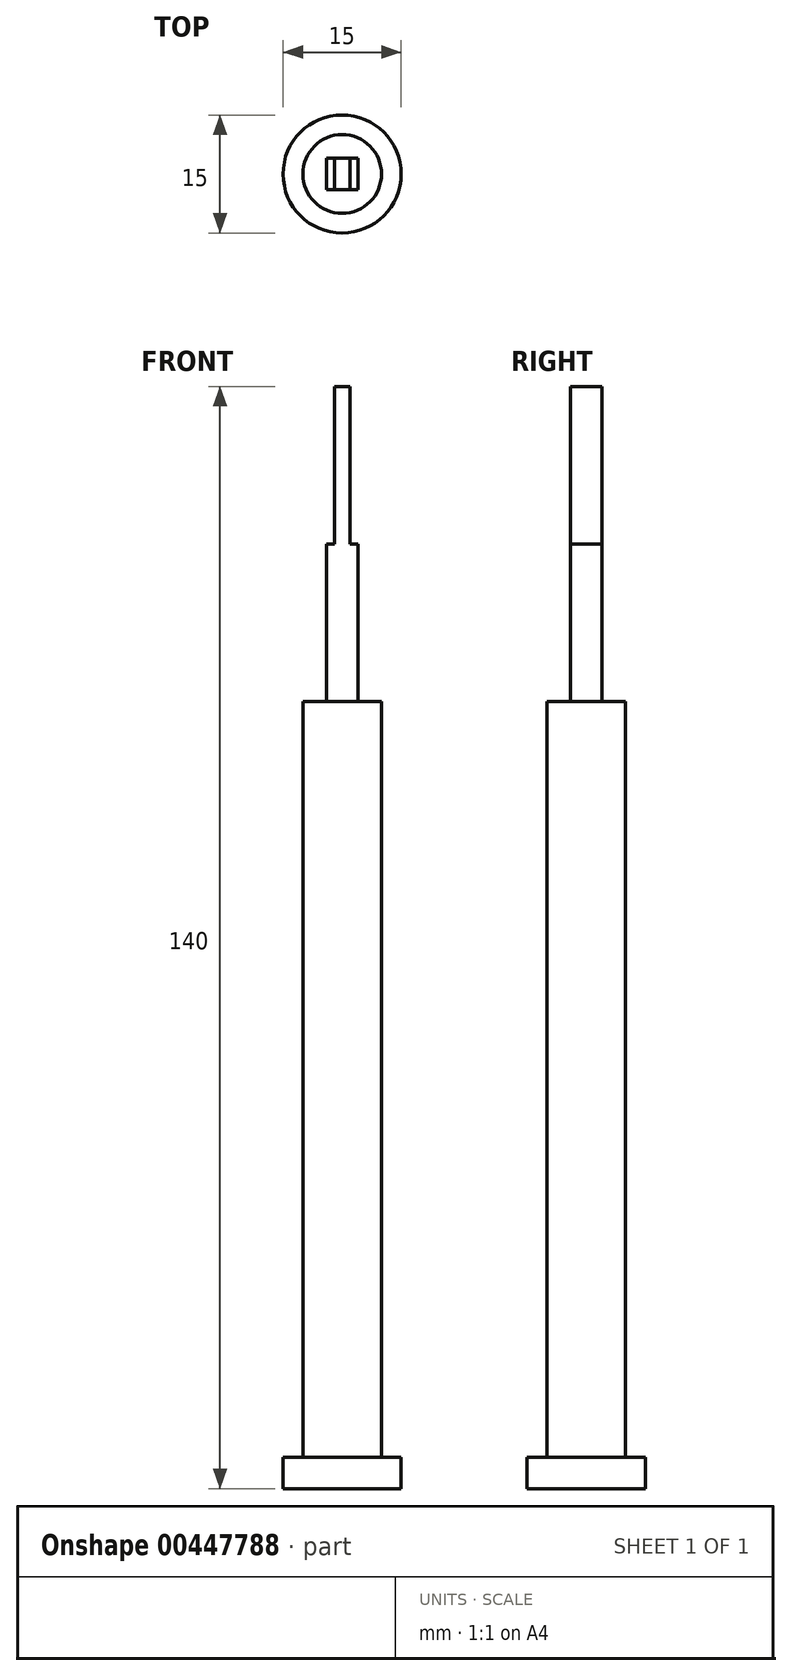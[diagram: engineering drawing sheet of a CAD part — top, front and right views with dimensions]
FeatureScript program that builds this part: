
annotation { "Feature Type Name" : "Feature", "Feature Type Description" : "" }
export const myFeature = defineFeature(function(context is Context, id is Id, definition is map)
    precondition{}
    {
        {
            var Q0;
            Q0=qCreatedBy(makeId("Top.planeOp"),FACE);
            var sketch = newSketch(context, id + "F0", { "sketchPlane" : qUnion([Q0])});
            skCircle(sketch, "E0", {"center": v(0, 0) * mm, "radius": 7.5 * mm});
            skSolve(sketch);
        }
        {
            var Q0;
            Q0=qSketchRegion(id+"F0",true);
            extrude(context, id + "F1", {"entities" : qUnion([Q0]), "depth" : 4 * mm});
        }
        {
            var Q0;
            Q0=qCreatedBy(makeId("Top.planeOp"),FACE);
            var sketch = newSketch(context, id + "F2", { "sketchPlane" : qUnion([Q0])});
            skCircle(sketch, "E1", {"center": v(0, 0) * mm, "radius": 5 * mm});
            skSolve(sketch);
        }
        {
            var Q0;
            Q0=qSketchRegion(id+"F2",true);
            extrude(context, id + "F3", {"entities" : qUnion([Q0]), "operationType" : NewBodyOperationType.ADD, "depth" : 100 * mm});
        }
        {
            var Q0;
            Q0=makeQuery(id+"F3.opExtrude","CAP_FACE",FACE,{"disambiguationData":[OSD([sQuery(id+"F2.wireOp",EDGE,"E1")])],"isStart":false});
            var sketch = newSketch(context, id + "F4", { "sketchPlane" : qUnion([Q0])});
            skLineSegment(sketch, "E2.bottom", {"start": v(-2, 2) * mm, "end": v(2, 2) * mm});
            skLineSegment(sketch, "E2.top", {"start": v(-2, -2) * mm, "end": v(2, -2) * mm});
            skLineSegment(sketch, "E2.left", {"start": v(-2, 2) * mm, "end": v(-2, -2) * mm});
            skLineSegment(sketch, "E2.right", {"start": v(2, 2) * mm, "end": v(2, -2) * mm});
            skSolve(sketch);
        }
        {
            var Q0;
            Q0=makeQuery(id+"F4.imprint","IMPRINT",FACE,{"disambiguationData":[TD([[makeQuery(id+"F4.imprint","IMPRINT",EDGE,{"derivedFrom":sQuery(id+"F4.wireOp",EDGE,"E2.bottom")}),-1.0]])]});
            extrude(context, id + "F5", {"entities" : qUnion([Q0]), "operationType" : NewBodyOperationType.ADD, "depth" : 20 * mm});
        }
        {
            var Q0;
            Q0=makeQuery(id+"F5.opExtrude","CAP_FACE",FACE,{"disambiguationData":[OSD([sQuery(id+"F4.wireOp",EDGE,"E2.bottom"),sQuery(id+"F4.wireOp",EDGE,"E2.top"),sQuery(id+"F4.wireOp",EDGE,"E2.left"),sQuery(id+"F4.wireOp",EDGE,"E2.right")])],"isStart":false});
            var sketch = newSketch(context, id + "F6", { "sketchPlane" : qUnion([Q0])});
            skLineSegment(sketch, "E3.bottom", {"start": v(-1, 2) * mm, "end": v(1, 2) * mm});
            skLineSegment(sketch, "E3.top", {"start": v(-1, -2) * mm, "end": v(1, -2) * mm});
            skLineSegment(sketch, "E3.left", {"start": v(-1, 2) * mm, "end": v(-1, -2) * mm});
            skLineSegment(sketch, "E3.right", {"start": v(1, 2) * mm, "end": v(1, -2) * mm});
            skSolve(sketch);
        }
        {
            var Q0;
            Q0=qSketchRegion(id+"F6",true);
            extrude(context, id + "F7", {"entities" : qUnion([Q0]), "operationType" : NewBodyOperationType.ADD, "depth" : 20 * mm});
        }
    });
